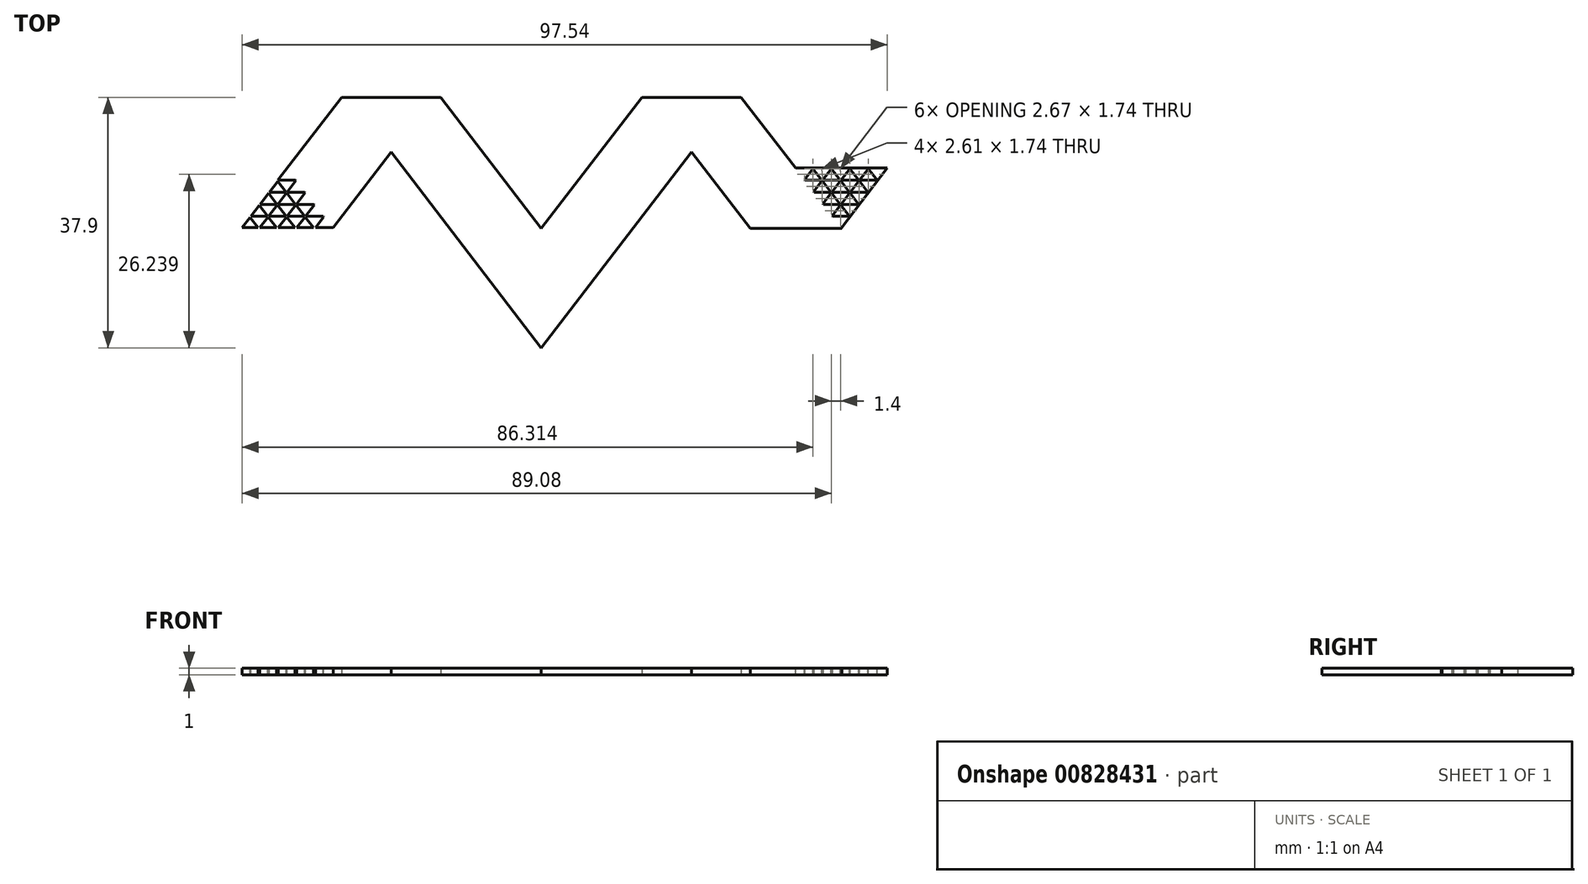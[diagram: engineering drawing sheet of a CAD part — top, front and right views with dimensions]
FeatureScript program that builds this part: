
annotation { "Feature Type Name" : "Feature", "Feature Type Description" : "" }
export const myFeature = defineFeature(function(context is Context, id is Id, definition is map)
    precondition{}
    {
        {
            var Q0;
            Q0=qCreatedBy(makeId("Top.planeOp"),FACE);
            var sketch = newSketch(context, id + "F0", { "sketchPlane" : qUnion([Q0])});
            skLineSegment(sketch, "E0", {"start": v(0, 0) * mm, "end": v(-15.22, 19.83) * mm});
            skLineSegment(sketch, "E1", {"start": v(-15.22, 19.83) * mm, "end": v(-30.22, 19.83) * mm});
            skLineSegment(sketch, "E2", {"start": v(-30.22, 19.83) * mm, "end": v(-45.44, 0) * mm});
            skLineSegment(sketch, "E3", {"start": v(-45.44, 0) * mm, "end": v(-30.44, 0) * mm});
            skPoint(sketch, "E4.endSnap0", {"position": v(-22.72, 19.83) * mm});
            skLineSegment(sketch, "E5.0", {"start": v(1.4, -19.9) * mm, "end": v(-23.55, 12.62) * mm});
            skLineSegment(sketch, "E6.0", {"start": v(-21.05, 13.7) * mm, "end": v(-36.27, -6.12) * mm});
            skLineSegment(sketch, "E7.MirrorCS", {"start": v(21.05, 13.7) * mm, "end": v(36.27, -6.12) * mm});
            skPoint(sketch, "E8.MirrorP", {"position": v(22.72, 19.83) * mm});
            skLineSegment(sketch, "E9.MirrorCS", {"start": v(45.44, 0) * mm, "end": v(30.44, 0) * mm});
            skLineSegment(sketch, "E10.MirrorCS", {"start": v(15.22, 19.83) * mm, "end": v(30.22, 19.83) * mm});
            skLineSegment(sketch, "E11.MirrorCS", {"start": v(-1.4, -19.9) * mm, "end": v(23.55, 12.62) * mm});
            skLineSegment(sketch, "E12.MirrorCS", {"start": v(0, 0) * mm, "end": v(15.22, 19.83) * mm});
            skLineSegment(sketch, "E13.MirrorCS", {"start": v(30.22, 19.83) * mm, "end": v(45.44, 0) * mm});
            skSolve(sketch);
        }
        {
            var Q0;
            Q0=makeQuery(id+"F0.imprint","IMPRINT",FACE,{"disambiguationData":[TD([[makeQuery(id+"F0.imprint","IMPRINT",EDGE,{"derivedFrom":sQuery(id+"F0.wireOp",EDGE,"E0")}),1.0]])]});
            extrude(context, id + "F1", {"entities" : qUnion([Q0]), "depth" : 1 * mm, "offsetDistance" : 25 * mm});
        }
        {
            var Q0;
            Q0=makeQuery(id+"F1.opExtrude","CAP_FACE",FACE,{"disambiguationData":[OSD([sQuery(id+"F0.wireOp",EDGE,"E0"),sQuery(id+"F0.wireOp",EDGE,"E1"),sQuery(id+"F0.wireOp",EDGE,"E2"),sQuery(id+"F0.wireOp",EDGE,"E3"),sQuery(id+"F0.wireOp",EDGE,"E5.0"),sQuery(id+"F0.wireOp",EDGE,"E6.0"),sQuery(id+"F0.wireOp",EDGE,"E7.MirrorCS"),sQuery(id+"F0.wireOp",EDGE,"E9.MirrorCS"),sQuery(id+"F0.wireOp",EDGE,"E10.MirrorCS"),sQuery(id+"F0.wireOp",EDGE,"E11.MirrorCS"),sQuery(id+"F0.wireOp",EDGE,"E12.MirrorCS"),sQuery(id+"F0.wireOp",EDGE,"E13.MirrorCS")])],"isStart":false});
            var sketch = newSketch(context, id + "F2", { "sketchPlane" : qUnion([Q0])});
            skLineSegment(sketch, "E14.1", {"start": v(-30.22, 19.83) * mm, "end": v(-45.44, 0) * mm});
            skLineSegment(sketch, "E14.2", {"start": v(-45.44, 0) * mm, "end": v(-31.57, 0) * mm});
            skPoint(sketch, "E14.3", {"position": v(-38.5, 0) * mm});
            skLineSegment(sketch, "E15.0", {"start": v(-22.72, 11.54) * mm, "end": v(-31.57, 0) * mm});
            skLineSegment(sketch, "E16", {"start": v(-44.04, 0) * mm, "end": v(-44.04, 13.08) * mm, "construction": true});
            skLineSegment(sketch, "E17", {"start": v(-42.64, 0) * mm, "end": v(-42.64, 13.5) * mm, "construction": true});
            skLineSegment(sketch, "E18", {"start": v(-41.24, 0) * mm, "end": v(-41.24, 16.53) * mm, "construction": true});
            skLineSegment(sketch, "E19.MirrorCS", {"start": v(-57.86, 19.83) * mm, "end": v(-42.64, 0) * mm});
            skLineSegment(sketch, "E20.MirrorCS", {"start": v(-55.06, 19.83) * mm, "end": v(-39.84, 0) * mm});
            skLineSegment(sketch, "E21.MirrorCS", {"start": v(-52.26, 19.83) * mm, "end": v(-37.04, 0) * mm});
            skLineSegment(sketch, "E22", {"start": v(-44.04, 1.82) * mm, "end": v(-41.24, 1.82) * mm});
            skLineSegment(sketch, "E23", {"start": v(-42.64, 3.65) * mm, "end": v(-39.84, 3.65) * mm});
            skLineSegment(sketch, "E24", {"start": v(-39.84, 3.65) * mm, "end": v(-41.24, 1.82) * mm});
            skLineSegment(sketch, "E25", {"start": v(-41.24, 1.82) * mm, "end": v(-38.44, 1.82) * mm});
            skLineSegment(sketch, "E26", {"start": v(-39.84, 0) * mm, "end": v(-39.84, 8.29) * mm, "construction": true});
            skLineSegment(sketch, "E27", {"start": v(-38.44, 0) * mm, "end": v(-38.44, 8.1) * mm, "construction": true});
            skLineSegment(sketch, "E28.MirrorCS", {"start": v(-49.46, 19.83) * mm, "end": v(-34.24, 0) * mm});
            skLineSegment(sketch, "E29.MirrorCS", {"start": v(-46.66, 19.83) * mm, "end": v(-31.44, 0) * mm});
            skLineSegment(sketch, "E30", {"start": v(-42.64, 0) * mm, "end": v(-41.24, 1.82) * mm});
            skLineSegment(sketch, "E31", {"start": v(-39.84, 0) * mm, "end": v(-38.44, 1.82) * mm});
            skLineSegment(sketch, "E32", {"start": v(-39.84, 3.65) * mm, "end": v(-38.44, 5.47) * mm});
            skLineSegment(sketch, "E33", {"start": v(-38.44, 5.47) * mm, "end": v(-41.24, 5.47) * mm});
            skLineSegment(sketch, "E34", {"start": v(-39.84, 7.3) * mm, "end": v(-37.04, 7.3) * mm});
            skLineSegment(sketch, "E35", {"start": v(-37.04, 7.3) * mm, "end": v(-38.44, 5.47) * mm});
            skLineSegment(sketch, "E36", {"start": v(-35.64, 5.47) * mm, "end": v(-38.44, 5.47) * mm});
            skLineSegment(sketch, "E37", {"start": v(-35.64, 5.47) * mm, "end": v(-38.44, 1.82) * mm});
            skLineSegment(sketch, "E38", {"start": v(-39.84, 3.65) * mm, "end": v(-34.24, 3.65) * mm});
            skLineSegment(sketch, "E39", {"start": v(-34.24, 3.65) * mm, "end": v(-37.04, 0) * mm});
            skLineSegment(sketch, "E40", {"start": v(-38.44, 1.82) * mm, "end": v(-32.84, 1.82) * mm});
            skLineSegment(sketch, "E41", {"start": v(-32.84, 1.82) * mm, "end": v(-34.24, 0) * mm});
            skLineSegment(sketch, "E42.MirrorCS", {"start": v(42.5, 7.3) * mm, "end": v(45.3, 7.3) * mm});
            skLineSegment(sketch, "E43.MirrorCS", {"start": v(45.3, 3.65) * mm, "end": v(42.5, 3.65) * mm});
            skLineSegment(sketch, "E44.MirrorCS", {"start": v(43.9, 5.47) * mm, "end": v(42.5, 7.3) * mm});
            skLineSegment(sketch, "E45.MirrorCS", {"start": v(43.9, 5.47) * mm, "end": v(45.3, 3.65) * mm});
            skLineSegment(sketch, "E46.MirrorCS", {"start": v(39.7, 7.3) * mm, "end": v(42.5, 7.3) * mm});
            skLineSegment(sketch, "E47.MirrorCS", {"start": v(46.7, 1.82) * mm, "end": v(45.3, 3.65) * mm});
            skLineSegment(sketch, "E48.MirrorCS", {"start": v(43.9, 9.12) * mm, "end": v(45.3, 7.3) * mm});
            skLineSegment(sketch, "E49.MirrorCS", {"start": v(43.9, 1.82) * mm, "end": v(46.7, 1.82) * mm});
            skLineSegment(sketch, "E50.MirrorCS", {"start": v(41.1, 9.12) * mm, "end": v(42.5, 7.3) * mm});
            skLineSegment(sketch, "E51.MirrorCS", {"start": v(45.3, 7.3) * mm, "end": v(50.9, 7.3) * mm});
            skLineSegment(sketch, "E52.MirrorCS", {"start": v(48.1, 3.65) * mm, "end": v(45.3, 3.65) * mm});
            skLineSegment(sketch, "E53.MirrorCS", {"start": v(50.9, 7.3) * mm, "end": v(49.5, 9.12) * mm});
            skLineSegment(sketch, "E54.MirrorCS", {"start": v(43.9, 9.12) * mm, "end": v(43.9, 0.84) * mm, "construction": true});
            skLineSegment(sketch, "E55.MirrorCS", {"start": v(38.3, 9.12) * mm, "end": v(52.3, 9.12) * mm});
            skLineSegment(sketch, "E56.MirrorCS", {"start": v(49.5, 5.47) * mm, "end": v(46.7, 9.12) * mm});
            skLineSegment(sketch, "E57.MirrorCS", {"start": v(45.3, 9.12) * mm, "end": v(45.3, 1.03) * mm, "construction": true});
            skLineSegment(sketch, "E58.MirrorCS", {"start": v(48.1, 3.65) * mm, "end": v(45.3, 7.3) * mm});
            skLineSegment(sketch, "E59.MirrorCS", {"start": v(43.9, 5.47) * mm, "end": v(49.5, 5.47) * mm});
            skLineSegment(sketch, "E60.MirrorCS", {"start": v(42.5, 9.12) * mm, "end": v(42.5, 0) * mm, "construction": true});
            skLineSegment(sketch, "E61.MirrorCS", {"start": v(41.1, 5.47) * mm, "end": v(43.9, 5.47) * mm});
            skLineSegment(sketch, "E62.MirrorCS", {"start": v(22.72, 11.54) * mm, "end": v(31.57, 0) * mm});
            skLineSegment(sketch, "E63.MirrorCS", {"start": v(41.1, 9.12) * mm, "end": v(41.1, 5.47) * mm, "construction": true});
            skLineSegment(sketch, "E64.MirrorCS", {"start": v(41.1, 1.82) * mm, "end": v(46.7, 9.12) * mm});
            skLineSegment(sketch, "E65.MirrorCS", {"start": v(53.52, -10.71) * mm, "end": v(38.3, 9.12) * mm});
            skLineSegment(sketch, "E66.MirrorCS", {"start": v(42.5, 0) * mm, "end": v(49.5, 9.12) * mm});
            skLineSegment(sketch, "E67.MirrorCS", {"start": v(39.7, 7.3) * mm, "end": v(41.1, 9.12) * mm});
            skLineSegment(sketch, "E68.MirrorCS", {"start": v(39.7, 9.12) * mm, "end": v(39.7, 7.3) * mm, "construction": true});
            skPoint(sketch, "E69.MirrorP", {"position": v(45.24, 9.12) * mm});
            skLineSegment(sketch, "E70.MirrorCS", {"start": v(45.3, 0) * mm, "end": v(52.3, 9.12) * mm});
            skLineSegment(sketch, "E71.MirrorCS", {"start": v(41.1, 5.47) * mm, "end": v(43.9, 9.12) * mm});
            skPoint(sketch, "E72.orphan", {"position": v(46.66, 19.83) * mm});
            skPoint(sketch, "E73.orphan", {"position": v(49.46, 19.83) * mm});
            skPoint(sketch, "E74.orphan", {"position": v(52.26, 19.83) * mm});
            skPoint(sketch, "E75.orphan", {"position": v(55.06, 19.83) * mm});
            skPoint(sketch, "E76.orphan", {"position": v(57.86, 19.83) * mm});
            skPoint(sketch, "E77.orphan", {"position": v(41.24, 16.53) * mm});
            skPoint(sketch, "E78.orphan", {"position": v(41.1, -4.38) * mm});
            skPoint(sketch, "E79.orphan", {"position": v(44.04, 13.08) * mm});
            skLineSegment(sketch, "E80", {"start": v(45.3, 0) * mm, "end": v(38.3, 9.12) * mm});
            skLineSegment(sketch, "E81.0", {"start": v(-45.24, 0.1) * mm, "end": v(-31.5, 0.1) * mm});
            skLineSegment(sketch, "E81.1", {"start": v(-30.14, 19.77) * mm, "end": v(-45.24, 0.1) * mm});
            skLineSegment(sketch, "E82.0", {"start": v(-57.94, 19.77) * mm, "end": v(-42.72, -0.06) * mm});
            skLineSegment(sketch, "E83.0", {"start": v(-55.14, 19.77) * mm, "end": v(-39.92, -0.06) * mm});
            skLineSegment(sketch, "E84.0", {"start": v(-52.34, 19.77) * mm, "end": v(-37.12, -0.06) * mm});
            skLineSegment(sketch, "E85.0", {"start": v(-49.54, 19.77) * mm, "end": v(-34.32, -0.06) * mm});
            skLineSegment(sketch, "E86.0", {"start": v(-46.74, 19.77) * mm, "end": v(-31.52, -0.06) * mm});
            skLineSegment(sketch, "E87.0", {"start": v(-38.44, 5.57) * mm, "end": v(-41.24, 5.57) * mm});
            skLineSegment(sketch, "E87.1", {"start": v(-35.64, 5.57) * mm, "end": v(-38.44, 5.57) * mm});
            skLineSegment(sketch, "E88.0", {"start": v(-39.84, 3.55) * mm, "end": v(-34.24, 3.55) * mm});
            skLineSegment(sketch, "E88.1", {"start": v(-42.64, 3.55) * mm, "end": v(-39.84, 3.55) * mm});
            skLineSegment(sketch, "E89.0", {"start": v(-38.44, 1.72) * mm, "end": v(-32.84, 1.72) * mm});
            skLineSegment(sketch, "E89.1", {"start": v(-41.24, 1.72) * mm, "end": v(-38.44, 1.72) * mm});
            skLineSegment(sketch, "E89.2", {"start": v(-44.04, 1.72) * mm, "end": v(-41.24, 1.72) * mm});
            skLineSegment(sketch, "E90.0", {"start": v(41.02, 9.06) * mm, "end": v(46.64, 1.74) * mm});
            skLineSegment(sketch, "E91.0", {"start": v(43.82, 9.06) * mm, "end": v(48.04, 3.57) * mm});
            skLineSegment(sketch, "E92.0", {"start": v(49.42, 5.41) * mm, "end": v(46.62, 9.06) * mm});
            skLineSegment(sketch, "E93.0", {"start": v(50.82, 7.24) * mm, "end": v(49.42, 9.06) * mm});
            skSolve(sketch);
        }
        {
            var Q0;
            {var subQ0=sQuery(id+"F2.wireOp",EDGE,"E81.0");var subQ3=sQuery(id+"F2.wireOp",EDGE,"E31");var subQ4=makeQuery(id+"F2.imprint","INTERSECT",VERTEX,{"derivedFrom":[subQ3,subQ0]});Q0=makeQuery(id+"F2.imprint","IMPRINT",FACE,{"disambiguationData":[TD([[makeQuery(id+"F2.imprint","IMPRINT",EDGE,{"disambiguationData":[TD([[subQ4,-1.0]])],"derivedFrom":subQ3}),1.0]])]});}
            var Q1;
            {var subQ3=sQuery(id+"F2.wireOp",EDGE,"E33");var subQ7=sQuery(id+"F2.wireOp",EDGE,"E85.0");var subQ9=makeQuery(id+"F2.imprint","INTERSECT",VERTEX,{"derivedFrom":[subQ3,subQ7]});Q1=makeQuery(id+"F2.imprint","IMPRINT",FACE,{"disambiguationData":[TD([[makeQuery(id+"F2.imprint","IMPRINT",EDGE,{"disambiguationData":[TD([[subQ9,-1.0]])],"derivedFrom":subQ3}),1.0]])]});}
            var Q2;
            {var subQ0=sQuery(id+"F2.wireOp",EDGE,"E81.1");var subQ3=sQuery(id+"F2.wireOp",EDGE,"E34");var subQ4=makeQuery(id+"F2.imprint","INTERSECT",VERTEX,{"derivedFrom":[subQ3,subQ0]});Q2=makeQuery(id+"F2.imprint","IMPRINT",FACE,{"disambiguationData":[TD([[makeQuery(id+"F2.imprint","IMPRINT",EDGE,{"disambiguationData":[TD([[subQ4,-1.0]])],"derivedFrom":subQ3}),-1.0]])]});}
            var Q3;
            {var subQ0=sQuery(id+"F2.wireOp",EDGE,"E36");var subQ5=sQuery(id+"F2.wireOp",EDGE,"E86.0");var subQ6=makeQuery(id+"F2.imprint","INTERSECT",VERTEX,{"derivedFrom":[subQ0,subQ5]});Q3=makeQuery(id+"F2.imprint","IMPRINT",FACE,{"disambiguationData":[TD([[makeQuery(id+"F2.imprint","IMPRINT",EDGE,{"disambiguationData":[TD([[subQ6,-1.0]])],"derivedFrom":subQ5}),-1.0]])]});}
            var Q4;
            {var subQ0=sQuery(id+"F2.wireOp",EDGE,"E89.2");var subQ1=sQuery(id+"F2.wireOp",EDGE,"E19.MirrorCS");var subQ2=makeQuery(id+"F2.imprint","INTERSECT",VERTEX,{"derivedFrom":[subQ1,subQ0]});Q4=makeQuery(id+"F2.imprint","IMPRINT",FACE,{"disambiguationData":[TD([[makeQuery(id+"F2.imprint","IMPRINT",EDGE,{"disambiguationData":[TD([[subQ2,-1.0]])],"derivedFrom":subQ1}),1.0]])]});}
            var Q5;
            {var subQ1=sQuery(id+"F2.wireOp",EDGE,"E20.MirrorCS");var subQ3=sQuery(id+"F2.wireOp",EDGE,"E88.1");var subQ4=makeQuery(id+"F2.imprint","INTERSECT",VERTEX,{"derivedFrom":[subQ1,subQ3]});Q5=makeQuery(id+"F2.imprint","IMPRINT",FACE,{"disambiguationData":[TD([[makeQuery(id+"F2.imprint","IMPRINT",EDGE,{"disambiguationData":[TD([[subQ4,-1.0]])],"derivedFrom":subQ3}),-1.0]])]});}
            var Q6;
            {var subQ1=sQuery(id+"F2.wireOp",EDGE,"E21.MirrorCS");var subQ3=sQuery(id+"F2.wireOp",EDGE,"E88.0");var subQ4=makeQuery(id+"F2.imprint","INTERSECT",VERTEX,{"derivedFrom":[subQ1,subQ3]});Q6=makeQuery(id+"F2.imprint","IMPRINT",FACE,{"disambiguationData":[TD([[makeQuery(id+"F2.imprint","IMPRINT",EDGE,{"disambiguationData":[TD([[subQ4,-1.0]])],"derivedFrom":subQ3}),-1.0]])]});}
            var Q7;
            {var subQ0=sQuery(id+"F2.wireOp",EDGE,"E89.0");var subQ1=sQuery(id+"F2.wireOp",EDGE,"E21.MirrorCS");var subQ2=makeQuery(id+"F2.imprint","INTERSECT",VERTEX,{"derivedFrom":[subQ1,subQ0]});Q7=makeQuery(id+"F2.imprint","IMPRINT",FACE,{"disambiguationData":[TD([[makeQuery(id+"F2.imprint","IMPRINT",EDGE,{"disambiguationData":[TD([[subQ2,-1.0]])],"derivedFrom":subQ1}),1.0]])]});}
            var Q8;
            {var subQ0=sQuery(id+"F2.wireOp",EDGE,"E88.0");var subQ1=sQuery(id+"F2.wireOp",EDGE,"E28.MirrorCS");var subQ2=makeQuery(id+"F2.imprint","INTERSECT",VERTEX,{"derivedFrom":[subQ1,subQ0]});Q8=makeQuery(id+"F2.imprint","IMPRINT",FACE,{"disambiguationData":[TD([[makeQuery(id+"F2.imprint","IMPRINT",EDGE,{"disambiguationData":[TD([[subQ2,-1.0]])],"derivedFrom":subQ0}),-1.0]])]});}
            var Q9;
            {var subQ0=sQuery(id+"F2.wireOp",EDGE,"E89.0");var subQ1=sQuery(id+"F2.wireOp",EDGE,"E28.MirrorCS");var subQ2=makeQuery(id+"F2.imprint","INTERSECT",VERTEX,{"derivedFrom":[subQ1,subQ0]});Q9=makeQuery(id+"F2.imprint","IMPRINT",FACE,{"disambiguationData":[TD([[makeQuery(id+"F2.imprint","IMPRINT",EDGE,{"disambiguationData":[TD([[subQ2,-1.0]])],"derivedFrom":subQ1}),1.0]])]});}
            extrude(context, id + "F3", {"entities" : qUnion([Q0, Q1, Q2, Q3, Q4, Q5, Q6, Q7, Q8, Q9]), "operationType" : NewBodyOperationType.REMOVE, "oppositeDirection" : true, "depth" : 25 * mm, "offsetDistance" : 25 * mm});
        }
        {
            var Q0;
            {var subQ0=sQuery(id+"F2.wireOp",EDGE,"E90.0");var subQ1=sQuery(id+"F2.wireOp",EDGE,"E49.MirrorCS");var subQ2=makeQuery(id+"F2.imprint","INTERSECT",VERTEX,{"derivedFrom":[subQ1,subQ0]});Q0=makeQuery(id+"F2.imprint","IMPRINT",FACE,{"disambiguationData":[TD([[makeQuery(id+"F2.imprint","IMPRINT",EDGE,{"disambiguationData":[TD([[subQ2,1.0]])],"derivedFrom":subQ1}),-1.0]])]});}
            var Q1;
            {var subQ0=sQuery(id+"F2.wireOp",EDGE,"E90.0");var subQ1=sQuery(id+"F2.wireOp",EDGE,"E43.MirrorCS");var subQ2=makeQuery(id+"F2.imprint","INTERSECT",VERTEX,{"derivedFrom":[subQ1,subQ0]});Q1=makeQuery(id+"F2.imprint","IMPRINT",FACE,{"disambiguationData":[TD([[makeQuery(id+"F2.imprint","IMPRINT",EDGE,{"disambiguationData":[TD([[subQ2,-1.0]])],"derivedFrom":subQ1}),1.0]])]});}
            var Q2;
            {var subQ0=sQuery(id+"F2.wireOp",EDGE,"E90.0");var subQ1=sQuery(id+"F2.wireOp",EDGE,"E61.MirrorCS");var subQ2=makeQuery(id+"F2.imprint","INTERSECT",VERTEX,{"derivedFrom":[subQ1,subQ0]});Q2=makeQuery(id+"F2.imprint","IMPRINT",FACE,{"disambiguationData":[TD([[makeQuery(id+"F2.imprint","IMPRINT",EDGE,{"disambiguationData":[TD([[subQ2,1.0]])],"derivedFrom":subQ1}),-1.0]])]});}
            var Q3;
            {var subQ0=sQuery(id+"F2.wireOp",EDGE,"E90.0");var subQ1=sQuery(id+"F2.wireOp",EDGE,"E46.MirrorCS");var subQ2=makeQuery(id+"F2.imprint","INTERSECT",VERTEX,{"derivedFrom":[subQ1,subQ0]});Q3=makeQuery(id+"F2.imprint","IMPRINT",FACE,{"disambiguationData":[TD([[makeQuery(id+"F2.imprint","IMPRINT",EDGE,{"disambiguationData":[TD([[subQ2,1.0]])],"derivedFrom":subQ1}),-1.0]])]});}
            var Q4;
            {var subQ0=sQuery(id+"F2.wireOp",EDGE,"E67.MirrorCS");var subQ5=makeQuery(id+"F2.imprint","INTERSECT",VERTEX,{"derivedFrom":[subQ0,sQuery(id+"F2.wireOp",EDGE,"E90.0")]});Q4=makeQuery(id+"F2.imprint","IMPRINT",FACE,{"disambiguationData":[TD([[makeQuery(id+"F2.imprint","IMPRINT",EDGE,{"disambiguationData":[TD([[subQ5,1.0]])],"derivedFrom":subQ0}),1.0]])]});}
            var Q5;
            {var subQ0=sQuery(id+"F2.wireOp",EDGE,"E50.MirrorCS");Q5=makeQuery(id+"F2.imprint","IMPRINT",FACE,{"disambiguationData":[TD([[makeQuery(id+"F2.imprint","IMPRINT",EDGE,{"derivedFrom":subQ0}),1.0]])]});}
            var Q6;
            {var subQ0=sQuery(id+"F2.wireOp",EDGE,"E44.MirrorCS");Q6=makeQuery(id+"F2.imprint","IMPRINT",FACE,{"disambiguationData":[TD([[makeQuery(id+"F2.imprint","IMPRINT",EDGE,{"derivedFrom":subQ0}),-1.0]])]});}
            var Q7;
            {var subQ0=sQuery(id+"F2.wireOp",EDGE,"E48.MirrorCS");Q7=makeQuery(id+"F2.imprint","IMPRINT",FACE,{"disambiguationData":[TD([[makeQuery(id+"F2.imprint","IMPRINT",EDGE,{"derivedFrom":subQ0}),1.0]])]});}
            var Q8;
            {var subQ0=sQuery(id+"F2.wireOp",EDGE,"E66.MirrorCS");var subQ5=makeQuery(id+"F2.imprint","INTERSECT",VERTEX,{"derivedFrom":[subQ0,sQuery(id+"F2.wireOp",EDGE,"E93.0")]});Q8=makeQuery(id+"F2.imprint","IMPRINT",FACE,{"disambiguationData":[TD([[makeQuery(id+"F2.imprint","IMPRINT",EDGE,{"disambiguationData":[TD([[subQ5,1.0]])],"derivedFrom":subQ0}),1.0]])]});}
            var Q9;
            {var subQ0=sQuery(id+"F2.wireOp",EDGE,"E53.MirrorCS");Q9=makeQuery(id+"F2.imprint","IMPRINT",FACE,{"disambiguationData":[TD([[makeQuery(id+"F2.imprint","IMPRINT",EDGE,{"derivedFrom":subQ0}),-1.0]])]});}
            var Q10;
            {var subQ0=sQuery(id+"F2.wireOp",EDGE,"E51.MirrorCS");var subQ1=makeQuery(id+"F2.imprint","INTERSECT",VERTEX,{"derivedFrom":[subQ0,sQuery(id+"F2.wireOp",EDGE,"E93.0")]});Q10=makeQuery(id+"F2.imprint","IMPRINT",FACE,{"disambiguationData":[TD([[makeQuery(id+"F2.imprint","IMPRINT",EDGE,{"disambiguationData":[TD([[subQ1,1.0]])],"derivedFrom":subQ0}),-1.0]])]});}
            var Q11;
            {var subQ3=sQuery(id+"F2.wireOp",EDGE,"E59.MirrorCS");var subQ6=makeQuery(id+"F2.imprint","INTERSECT",VERTEX,{"derivedFrom":[subQ3,sQuery(id+"F2.wireOp",EDGE,"E92.0")]});Q11=makeQuery(id+"F2.imprint","IMPRINT",FACE,{"disambiguationData":[TD([[makeQuery(id+"F2.imprint","IMPRINT",EDGE,{"disambiguationData":[TD([[subQ6,1.0]])],"derivedFrom":subQ3}),-1.0]])]});}
            var Q12;
            {var subQ1=sQuery(id+"F2.wireOp",EDGE,"E51.MirrorCS");var subQ3=sQuery(id+"F2.wireOp",EDGE,"E92.0");var subQ4=makeQuery(id+"F2.imprint","INTERSECT",VERTEX,{"derivedFrom":[subQ1,subQ3]});Q12=makeQuery(id+"F2.imprint","IMPRINT",FACE,{"disambiguationData":[TD([[makeQuery(id+"F2.imprint","IMPRINT",EDGE,{"disambiguationData":[TD([[subQ4,1.0]])],"derivedFrom":subQ3}),1.0]])]});}
            var Q13;
            {var subQ0=sQuery(id+"F2.wireOp",EDGE,"E45.MirrorCS");Q13=makeQuery(id+"F2.imprint","IMPRINT",FACE,{"disambiguationData":[TD([[makeQuery(id+"F2.imprint","IMPRINT",EDGE,{"derivedFrom":subQ0}),1.0]])]});}
            var Q14;
            {var subQ0=sQuery(id+"F2.wireOp",EDGE,"E47.MirrorCS");Q14=makeQuery(id+"F2.imprint","IMPRINT",FACE,{"disambiguationData":[TD([[makeQuery(id+"F2.imprint","IMPRINT",EDGE,{"derivedFrom":subQ0}),-1.0]])]});}
            var Q15;
            {var subQ0=sQuery(id+"F2.wireOp",EDGE,"E47.MirrorCS");Q15=makeQuery(id+"F2.imprint","IMPRINT",FACE,{"disambiguationData":[TD([[makeQuery(id+"F2.imprint","IMPRINT",EDGE,{"derivedFrom":subQ0}),1.0]])]});}
            var Q16;
            {var subQ1=sQuery(id+"F2.wireOp",EDGE,"E43.MirrorCS");var subQ3=sQuery(id+"F2.wireOp",EDGE,"E90.0");var subQ4=makeQuery(id+"F2.imprint","INTERSECT",VERTEX,{"derivedFrom":[subQ1,subQ3]});Q16=makeQuery(id+"F2.imprint","IMPRINT",FACE,{"disambiguationData":[TD([[makeQuery(id+"F2.imprint","IMPRINT",EDGE,{"disambiguationData":[TD([[subQ4,-1.0]])],"derivedFrom":subQ3}),1.0]])]});}
            var Q17;
            {var subQ0=sQuery(id+"F2.wireOp",EDGE,"E45.MirrorCS");Q17=makeQuery(id+"F2.imprint","IMPRINT",FACE,{"disambiguationData":[TD([[makeQuery(id+"F2.imprint","IMPRINT",EDGE,{"derivedFrom":subQ0}),-1.0]])]});}
            var Q18;
            {var subQ0=sQuery(id+"F2.wireOp",EDGE,"E70.MirrorCS");var subQ3=sQuery(id+"F2.wireOp",EDGE,"E90.0");var subQ5=makeQuery(id+"F2.imprint","INTERSECT",VERTEX,{"derivedFrom":[subQ0,subQ3]});Q18=makeQuery(id+"F2.imprint","IMPRINT",FACE,{"disambiguationData":[TD([[makeQuery(id+"F2.imprint","IMPRINT",EDGE,{"disambiguationData":[TD([[subQ5,1.0]])],"derivedFrom":subQ3}),1.0]])]});}
            var Q19;
            {var subQ0=sQuery(id+"F2.wireOp",EDGE,"E44.MirrorCS");Q19=makeQuery(id+"F2.imprint","IMPRINT",FACE,{"disambiguationData":[TD([[makeQuery(id+"F2.imprint","IMPRINT",EDGE,{"derivedFrom":subQ0}),1.0]])]});}
            var Q20;
            {var subQ1=sQuery(id+"F2.wireOp",EDGE,"E61.MirrorCS");var subQ3=sQuery(id+"F2.wireOp",EDGE,"E90.0");var subQ4=makeQuery(id+"F2.imprint","INTERSECT",VERTEX,{"derivedFrom":[subQ1,subQ3]});Q20=makeQuery(id+"F2.imprint","IMPRINT",FACE,{"disambiguationData":[TD([[makeQuery(id+"F2.imprint","IMPRINT",EDGE,{"disambiguationData":[TD([[subQ4,-1.0]])],"derivedFrom":subQ3}),1.0]])]});}
            var Q21;
            {var subQ1=sQuery(id+"F2.wireOp",EDGE,"E52.MirrorCS");var subQ3=sQuery(id+"F2.wireOp",EDGE,"E91.0");var subQ4=makeQuery(id+"F2.imprint","INTERSECT",VERTEX,{"derivedFrom":[subQ1,subQ3]});Q21=makeQuery(id+"F2.imprint","IMPRINT",FACE,{"disambiguationData":[TD([[makeQuery(id+"F2.imprint","IMPRINT",EDGE,{"disambiguationData":[TD([[subQ4,1.0]])],"derivedFrom":subQ3}),1.0]])]});}
            var Q22;
            {var subQ0=sQuery(id+"F2.wireOp",EDGE,"E91.0");var subQ1=sQuery(id+"F2.wireOp",EDGE,"E59.MirrorCS");var subQ2=makeQuery(id+"F2.imprint","INTERSECT",VERTEX,{"derivedFrom":[subQ1,subQ0]});Q22=makeQuery(id+"F2.imprint","IMPRINT",FACE,{"disambiguationData":[TD([[makeQuery(id+"F2.imprint","IMPRINT",EDGE,{"disambiguationData":[TD([[subQ2,-1.0]])],"derivedFrom":subQ0}),1.0]])]});}
            var Q23;
            {var subQ3=sQuery(id+"F2.wireOp",EDGE,"E59.MirrorCS");var subQ5=sQuery(id+"F2.wireOp",EDGE,"E91.0");var subQ6=makeQuery(id+"F2.imprint","INTERSECT",VERTEX,{"derivedFrom":[subQ3,subQ5]});Q23=makeQuery(id+"F2.imprint","IMPRINT",FACE,{"disambiguationData":[TD([[makeQuery(id+"F2.imprint","IMPRINT",EDGE,{"disambiguationData":[TD([[subQ6,1.0]])],"derivedFrom":subQ5}),1.0]])]});}
            var Q24;
            {var subQ0=sQuery(id+"F2.wireOp",EDGE,"E70.MirrorCS");var subQ3=sQuery(id+"F2.wireOp",EDGE,"E91.0");var subQ5=makeQuery(id+"F2.imprint","INTERSECT",VERTEX,{"derivedFrom":[subQ0,subQ3]});Q24=makeQuery(id+"F2.imprint","IMPRINT",FACE,{"disambiguationData":[TD([[makeQuery(id+"F2.imprint","IMPRINT",EDGE,{"disambiguationData":[TD([[subQ5,1.0]])],"derivedFrom":subQ3}),1.0]])]});}
            var Q25;
            {var subQ0=sQuery(id+"F2.wireOp",EDGE,"E59.MirrorCS");var subQ5=sQuery(id+"F2.wireOp",EDGE,"E92.0");var subQ6=makeQuery(id+"F2.imprint","INTERSECT",VERTEX,{"derivedFrom":[subQ0,subQ5]});Q25=makeQuery(id+"F2.imprint","IMPRINT",FACE,{"disambiguationData":[TD([[makeQuery(id+"F2.imprint","IMPRINT",EDGE,{"disambiguationData":[TD([[subQ6,-1.0]])],"derivedFrom":subQ5}),-1.0]])]});}
            var Q26;
            {var subQ0=sQuery(id+"F2.wireOp",EDGE,"E50.MirrorCS");Q26=makeQuery(id+"F2.imprint","IMPRINT",FACE,{"disambiguationData":[TD([[makeQuery(id+"F2.imprint","IMPRINT",EDGE,{"derivedFrom":subQ0}),-1.0]])]});}
            var Q27;
            {var subQ1=sQuery(id+"F2.wireOp",EDGE,"E46.MirrorCS");var subQ3=sQuery(id+"F2.wireOp",EDGE,"E90.0");var subQ4=makeQuery(id+"F2.imprint","INTERSECT",VERTEX,{"derivedFrom":[subQ1,subQ3]});Q27=makeQuery(id+"F2.imprint","IMPRINT",FACE,{"disambiguationData":[TD([[makeQuery(id+"F2.imprint","IMPRINT",EDGE,{"disambiguationData":[TD([[subQ4,-1.0]])],"derivedFrom":subQ3}),1.0]])]});}
            var Q28;
            {var subQ0=sQuery(id+"F2.wireOp",EDGE,"E48.MirrorCS");Q28=makeQuery(id+"F2.imprint","IMPRINT",FACE,{"disambiguationData":[TD([[makeQuery(id+"F2.imprint","IMPRINT",EDGE,{"derivedFrom":subQ0}),-1.0]])]});}
            var Q29;
            {var subQ1=sQuery(id+"F2.wireOp",EDGE,"E42.MirrorCS");var subQ3=sQuery(id+"F2.wireOp",EDGE,"E91.0");var subQ4=makeQuery(id+"F2.imprint","INTERSECT",VERTEX,{"derivedFrom":[subQ1,subQ3]});Q29=makeQuery(id+"F2.imprint","IMPRINT",FACE,{"disambiguationData":[TD([[makeQuery(id+"F2.imprint","IMPRINT",EDGE,{"disambiguationData":[TD([[subQ4,-1.0]])],"derivedFrom":subQ3}),1.0]])]});}
            var Q30;
            {var subQ0=sQuery(id+"F2.wireOp",EDGE,"E92.0");var subQ5=sQuery(id+"F2.wireOp",EDGE,"E64.MirrorCS");var subQ7=makeQuery(id+"F2.imprint","INTERSECT",VERTEX,{"derivedFrom":[subQ5,subQ0]});Q30=makeQuery(id+"F2.imprint","IMPRINT",FACE,{"disambiguationData":[TD([[makeQuery(id+"F2.imprint","IMPRINT",EDGE,{"disambiguationData":[TD([[subQ7,1.0]])],"derivedFrom":subQ0}),-1.0]])]});}
            var Q31;
            {var subQ0=sQuery(id+"F2.wireOp",EDGE,"E92.0");var subQ1=sQuery(id+"F2.wireOp",EDGE,"E51.MirrorCS");var subQ2=makeQuery(id+"F2.imprint","INTERSECT",VERTEX,{"derivedFrom":[subQ1,subQ0]});Q31=makeQuery(id+"F2.imprint","IMPRINT",FACE,{"disambiguationData":[TD([[makeQuery(id+"F2.imprint","IMPRINT",EDGE,{"disambiguationData":[TD([[subQ2,1.0]])],"derivedFrom":subQ0}),-1.0]])]});}
            var Q32;
            {var subQ0=sQuery(id+"F2.wireOp",EDGE,"E53.MirrorCS");Q32=makeQuery(id+"F2.imprint","IMPRINT",FACE,{"disambiguationData":[TD([[makeQuery(id+"F2.imprint","IMPRINT",EDGE,{"derivedFrom":subQ0}),1.0]])]});}
            extrude(context, id + "F4", {"entities" : qUnion([Q0, Q1, Q2, Q3, Q4, Q5, Q6, Q7, Q8, Q9, Q10, Q11, Q12, Q13, Q14, Q15, Q16, Q17, Q18, Q19, Q20, Q21, Q22, Q23, Q24, Q25, Q26, Q27, Q28, Q29, Q30, Q31, Q32]), "operationType" : NewBodyOperationType.ADD, "oppositeDirection" : true, "depth" : 1 * mm, "offsetDistance" : 25 * mm});
        }
        {
            var Q0;
            {var subQ5=sQuery(id+"F2.wireOp",EDGE,"E14.2");var subQ6=sQuery(id+"F2.wireOp",EDGE,"E14.1");var subQ7=makeQuery(id+"F2.imprint","INTERSECT",VERTEX,{"derivedFrom":[subQ6,subQ5]});Q0=makeQuery(id+"F2.imprint","IMPRINT",FACE,{"disambiguationData":[TD([[makeQuery(id+"F2.imprint","IMPRINT",EDGE,{"disambiguationData":[TD([[subQ7,1.0]])],"derivedFrom":subQ6}),1.0]])]});}
            var Q1;
            {var subQ0=sQuery(id+"F2.wireOp",EDGE,"E81.1");var subQ1=makeQuery(id+"F2.imprint","INTERSECT",VERTEX,{"derivedFrom":[subQ0,sQuery(id+"F2.wireOp",EDGE,"E89.2")]});Q1=makeQuery(id+"F2.imprint","IMPRINT",FACE,{"disambiguationData":[TD([[makeQuery(id+"F2.imprint","IMPRINT",EDGE,{"disambiguationData":[TD([[subQ1,1.0]])],"derivedFrom":subQ0}),-1.0]])]});}
            var Q2;
            {var subQ1=sQuery(id+"F2.wireOp",EDGE,"E19.MirrorCS");var subQ3=sQuery(id+"F2.wireOp",EDGE,"E81.1");var subQ4=makeQuery(id+"F2.imprint","INTERSECT",VERTEX,{"derivedFrom":[subQ1,subQ3]});Q2=makeQuery(id+"F2.imprint","IMPRINT",FACE,{"disambiguationData":[TD([[makeQuery(id+"F2.imprint","IMPRINT",EDGE,{"disambiguationData":[TD([[subQ4,1.0]])],"derivedFrom":subQ3}),-1.0]])]});}
            var Q3;
            {var subQ0=sQuery(id+"F2.wireOp",EDGE,"E22");var subQ5=sQuery(id+"F2.wireOp",EDGE,"E81.1");var subQ6=makeQuery(id+"F2.imprint","INTERSECT",VERTEX,{"derivedFrom":[subQ0,subQ5]});Q3=makeQuery(id+"F2.imprint","IMPRINT",FACE,{"disambiguationData":[TD([[makeQuery(id+"F2.imprint","IMPRINT",EDGE,{"disambiguationData":[TD([[subQ6,1.0]])],"derivedFrom":subQ5}),-1.0]])]});}
            var Q4;
            {var subQ0=sQuery(id+"F2.wireOp",EDGE,"E19.MirrorCS");var subQ5=sQuery(id+"F2.wireOp",EDGE,"E81.0");var subQ6=makeQuery(id+"F2.imprint","INTERSECT",VERTEX,{"derivedFrom":[subQ0,subQ5]});Q4=makeQuery(id+"F2.imprint","IMPRINT",FACE,{"disambiguationData":[TD([[makeQuery(id+"F2.imprint","IMPRINT",EDGE,{"disambiguationData":[TD([[subQ6,1.0]])],"derivedFrom":subQ5}),-1.0]])]});}
            var Q5;
            {var subQ1=sQuery(id+"F2.wireOp",EDGE,"E19.MirrorCS");var subQ3=sQuery(id+"F2.wireOp",EDGE,"E81.0");var subQ4=makeQuery(id+"F2.imprint","INTERSECT",VERTEX,{"derivedFrom":[subQ1,subQ3]});Q5=makeQuery(id+"F2.imprint","IMPRINT",FACE,{"disambiguationData":[TD([[makeQuery(id+"F2.imprint","IMPRINT",EDGE,{"disambiguationData":[TD([[subQ4,-1.0]])],"derivedFrom":subQ3}),-1.0]])]});}
            var Q6;
            {var subQ0=sQuery(id+"F2.wireOp",EDGE,"E30");var subQ5=sQuery(id+"F2.wireOp",EDGE,"E81.0");var subQ6=makeQuery(id+"F2.imprint","INTERSECT",VERTEX,{"derivedFrom":[subQ0,subQ5]});Q6=makeQuery(id+"F2.imprint","IMPRINT",FACE,{"disambiguationData":[TD([[makeQuery(id+"F2.imprint","IMPRINT",EDGE,{"disambiguationData":[TD([[subQ6,-1.0]])],"derivedFrom":subQ5}),-1.0]])]});}
            var Q7;
            {var subQ0=sQuery(id+"F2.wireOp",EDGE,"E20.MirrorCS");var subQ5=sQuery(id+"F2.wireOp",EDGE,"E81.0");var subQ7=makeQuery(id+"F2.imprint","INTERSECT",VERTEX,{"derivedFrom":[subQ0,subQ5]});Q7=makeQuery(id+"F2.imprint","IMPRINT",FACE,{"disambiguationData":[TD([[makeQuery(id+"F2.imprint","IMPRINT",EDGE,{"disambiguationData":[TD([[subQ7,1.0]])],"derivedFrom":subQ5}),-1.0]])]});}
            var Q8;
            {var subQ1=sQuery(id+"F2.wireOp",EDGE,"E20.MirrorCS");var subQ3=sQuery(id+"F2.wireOp",EDGE,"E81.0");var subQ4=makeQuery(id+"F2.imprint","INTERSECT",VERTEX,{"derivedFrom":[subQ1,subQ3]});Q8=makeQuery(id+"F2.imprint","IMPRINT",FACE,{"disambiguationData":[TD([[makeQuery(id+"F2.imprint","IMPRINT",EDGE,{"disambiguationData":[TD([[subQ4,-1.0]])],"derivedFrom":subQ3}),-1.0]])]});}
            var Q9;
            {var subQ0=sQuery(id+"F2.wireOp",EDGE,"E31");var subQ5=sQuery(id+"F2.wireOp",EDGE,"E81.0");var subQ6=makeQuery(id+"F2.imprint","INTERSECT",VERTEX,{"derivedFrom":[subQ0,subQ5]});Q9=makeQuery(id+"F2.imprint","IMPRINT",FACE,{"disambiguationData":[TD([[makeQuery(id+"F2.imprint","IMPRINT",EDGE,{"disambiguationData":[TD([[subQ6,-1.0]])],"derivedFrom":subQ5}),-1.0]])]});}
            var Q10;
            {var subQ0=sQuery(id+"F2.wireOp",EDGE,"E81.1");var subQ1=makeQuery(id+"F2.imprint","INTERSECT",VERTEX,{"derivedFrom":[subQ0,sQuery(id+"F2.wireOp",EDGE,"E88.1")]});Q10=makeQuery(id+"F2.imprint","IMPRINT",FACE,{"disambiguationData":[TD([[makeQuery(id+"F2.imprint","IMPRINT",EDGE,{"disambiguationData":[TD([[subQ1,1.0]])],"derivedFrom":subQ0}),-1.0]])]});}
            var Q11;
            {var subQ1=sQuery(id+"F2.wireOp",EDGE,"E20.MirrorCS");var subQ3=sQuery(id+"F2.wireOp",EDGE,"E81.1");var subQ4=makeQuery(id+"F2.imprint","INTERSECT",VERTEX,{"derivedFrom":[subQ1,subQ3]});Q11=makeQuery(id+"F2.imprint","IMPRINT",FACE,{"disambiguationData":[TD([[makeQuery(id+"F2.imprint","IMPRINT",EDGE,{"disambiguationData":[TD([[subQ4,1.0]])],"derivedFrom":subQ3}),-1.0]])]});}
            var Q12;
            {var subQ0=sQuery(id+"F2.wireOp",EDGE,"E23");var subQ5=sQuery(id+"F2.wireOp",EDGE,"E81.1");var subQ6=makeQuery(id+"F2.imprint","INTERSECT",VERTEX,{"derivedFrom":[subQ0,subQ5]});Q12=makeQuery(id+"F2.imprint","IMPRINT",FACE,{"disambiguationData":[TD([[makeQuery(id+"F2.imprint","IMPRINT",EDGE,{"disambiguationData":[TD([[subQ6,1.0]])],"derivedFrom":subQ5}),-1.0]])]});}
            var Q13;
            {var subQ0=sQuery(id+"F2.wireOp",EDGE,"E21.MirrorCS");var subQ5=sQuery(id+"F2.wireOp",EDGE,"E81.1");var subQ7=makeQuery(id+"F2.imprint","INTERSECT",VERTEX,{"derivedFrom":[subQ0,subQ5]});Q13=makeQuery(id+"F2.imprint","IMPRINT",FACE,{"disambiguationData":[TD([[makeQuery(id+"F2.imprint","IMPRINT",EDGE,{"disambiguationData":[TD([[subQ7,-1.0]])],"derivedFrom":subQ5}),-1.0]])]});}
            var Q14;
            {var subQ1=sQuery(id+"F2.wireOp",EDGE,"E21.MirrorCS");var subQ3=sQuery(id+"F2.wireOp",EDGE,"E81.1");var subQ4=makeQuery(id+"F2.imprint","INTERSECT",VERTEX,{"derivedFrom":[subQ1,subQ3]});Q14=makeQuery(id+"F2.imprint","IMPRINT",FACE,{"disambiguationData":[TD([[makeQuery(id+"F2.imprint","IMPRINT",EDGE,{"disambiguationData":[TD([[subQ4,1.0]])],"derivedFrom":subQ3}),-1.0]])]});}
            var Q15;
            {var subQ0=sQuery(id+"F2.wireOp",EDGE,"E33");var subQ5=sQuery(id+"F2.wireOp",EDGE,"E81.1");var subQ6=makeQuery(id+"F2.imprint","INTERSECT",VERTEX,{"derivedFrom":[subQ0,subQ5]});Q15=makeQuery(id+"F2.imprint","IMPRINT",FACE,{"disambiguationData":[TD([[makeQuery(id+"F2.imprint","IMPRINT",EDGE,{"disambiguationData":[TD([[subQ6,1.0]])],"derivedFrom":subQ5}),-1.0]])]});}
            var Q16;
            {var subQ0=sQuery(id+"F2.wireOp",EDGE,"E85.0");var subQ1=sQuery(id+"F2.wireOp",EDGE,"E14.1");var subQ2=makeQuery(id+"F2.imprint","INTERSECT",VERTEX,{"derivedFrom":[subQ1,subQ0]});Q16=makeQuery(id+"F2.imprint","IMPRINT",FACE,{"disambiguationData":[TD([[makeQuery(id+"F2.imprint","IMPRINT",EDGE,{"disambiguationData":[TD([[subQ2,-1.0]])],"derivedFrom":subQ1}),1.0]])]});}
            var Q17;
            {var subQ0=sQuery(id+"F2.wireOp",EDGE,"E28.MirrorCS");var subQ5=sQuery(id+"F2.wireOp",EDGE,"E81.1");var subQ6=makeQuery(id+"F2.imprint","INTERSECT",VERTEX,{"derivedFrom":[subQ0,subQ5]});Q17=makeQuery(id+"F2.imprint","IMPRINT",FACE,{"disambiguationData":[TD([[makeQuery(id+"F2.imprint","IMPRINT",EDGE,{"disambiguationData":[TD([[subQ6,-1.0]])],"derivedFrom":subQ5}),-1.0]])]});}
            var Q18;
            {var subQ1=sQuery(id+"F2.wireOp",EDGE,"E28.MirrorCS");var subQ3=sQuery(id+"F2.wireOp",EDGE,"E81.1");var subQ4=makeQuery(id+"F2.imprint","INTERSECT",VERTEX,{"derivedFrom":[subQ1,subQ3]});Q18=makeQuery(id+"F2.imprint","IMPRINT",FACE,{"disambiguationData":[TD([[makeQuery(id+"F2.imprint","IMPRINT",EDGE,{"disambiguationData":[TD([[subQ4,1.0]])],"derivedFrom":subQ3}),-1.0]])]});}
            var Q19;
            {var subQ0=sQuery(id+"F2.wireOp",EDGE,"E21.MirrorCS");var subQ5=sQuery(id+"F2.wireOp",EDGE,"E81.0");var subQ6=makeQuery(id+"F2.imprint","INTERSECT",VERTEX,{"derivedFrom":[subQ0,subQ5]});Q19=makeQuery(id+"F2.imprint","IMPRINT",FACE,{"disambiguationData":[TD([[makeQuery(id+"F2.imprint","IMPRINT",EDGE,{"disambiguationData":[TD([[subQ6,1.0]])],"derivedFrom":subQ5}),-1.0]])]});}
            var Q20;
            {var subQ1=sQuery(id+"F2.wireOp",EDGE,"E21.MirrorCS");var subQ3=sQuery(id+"F2.wireOp",EDGE,"E81.0");var subQ4=makeQuery(id+"F2.imprint","INTERSECT",VERTEX,{"derivedFrom":[subQ1,subQ3]});Q20=makeQuery(id+"F2.imprint","IMPRINT",FACE,{"disambiguationData":[TD([[makeQuery(id+"F2.imprint","IMPRINT",EDGE,{"disambiguationData":[TD([[subQ4,-1.0]])],"derivedFrom":subQ3}),-1.0]])]});}
            var Q21;
            {var subQ0=sQuery(id+"F2.wireOp",EDGE,"E39");var subQ5=sQuery(id+"F2.wireOp",EDGE,"E81.0");var subQ6=makeQuery(id+"F2.imprint","INTERSECT",VERTEX,{"derivedFrom":[subQ0,subQ5]});Q21=makeQuery(id+"F2.imprint","IMPRINT",FACE,{"disambiguationData":[TD([[makeQuery(id+"F2.imprint","IMPRINT",EDGE,{"disambiguationData":[TD([[subQ6,-1.0]])],"derivedFrom":subQ5}),-1.0]])]});}
            var Q22;
            {var subQ0=sQuery(id+"F2.wireOp",EDGE,"E28.MirrorCS");var subQ5=sQuery(id+"F2.wireOp",EDGE,"E81.0");var subQ6=makeQuery(id+"F2.imprint","INTERSECT",VERTEX,{"derivedFrom":[subQ0,subQ5]});Q22=makeQuery(id+"F2.imprint","IMPRINT",FACE,{"disambiguationData":[TD([[makeQuery(id+"F2.imprint","IMPRINT",EDGE,{"disambiguationData":[TD([[subQ6,1.0]])],"derivedFrom":subQ5}),-1.0]])]});}
            var Q23;
            {var subQ1=sQuery(id+"F2.wireOp",EDGE,"E28.MirrorCS");var subQ3=sQuery(id+"F2.wireOp",EDGE,"E81.0");var subQ4=makeQuery(id+"F2.imprint","INTERSECT",VERTEX,{"derivedFrom":[subQ1,subQ3]});Q23=makeQuery(id+"F2.imprint","IMPRINT",FACE,{"disambiguationData":[TD([[makeQuery(id+"F2.imprint","IMPRINT",EDGE,{"disambiguationData":[TD([[subQ4,-1.0]])],"derivedFrom":subQ3}),-1.0]])]});}
            var Q24;
            {var subQ5=sQuery(id+"F2.wireOp",EDGE,"E14.2");var subQ7=sQuery(id+"F2.wireOp",EDGE,"E15.0");var subQ8=makeQuery(id+"F2.imprint","INTERSECT",VERTEX,{"derivedFrom":[subQ5,subQ7]});Q24=makeQuery(id+"F2.imprint","IMPRINT",FACE,{"disambiguationData":[TD([[makeQuery(id+"F2.imprint","IMPRINT",EDGE,{"disambiguationData":[TD([[subQ8,1.0]])],"derivedFrom":subQ7}),-1.0]])]});}
            var Q25;
            {var subQ0=sQuery(id+"F2.wireOp",EDGE,"E81.1");var subQ1=sQuery(id+"F2.wireOp",EDGE,"E19.MirrorCS");var subQ2=makeQuery(id+"F2.imprint","INTERSECT",VERTEX,{"derivedFrom":[subQ1,subQ0]});Q25=makeQuery(id+"F2.imprint","IMPRINT",FACE,{"disambiguationData":[TD([[makeQuery(id+"F2.imprint","IMPRINT",EDGE,{"disambiguationData":[TD([[subQ2,-1.0]])],"derivedFrom":subQ1}),1.0]])]});}
            var Q26;
            {var subQ1=sQuery(id+"F2.wireOp",EDGE,"E22");var subQ3=sQuery(id+"F2.wireOp",EDGE,"E83.0");var subQ4=makeQuery(id+"F2.imprint","INTERSECT",VERTEX,{"derivedFrom":[subQ1,subQ3]});Q26=makeQuery(id+"F2.imprint","IMPRINT",FACE,{"disambiguationData":[TD([[makeQuery(id+"F2.imprint","IMPRINT",EDGE,{"disambiguationData":[TD([[subQ4,-1.0]])],"derivedFrom":subQ3}),1.0]])]});}
            var Q27;
            {var subQ5=sQuery(id+"F2.wireOp",EDGE,"E83.0");var subQ6=sQuery(id+"F2.wireOp",EDGE,"E30");var subQ7=makeQuery(id+"F2.imprint","INTERSECT",VERTEX,{"derivedFrom":[subQ6,subQ5]});Q27=makeQuery(id+"F2.imprint","IMPRINT",FACE,{"disambiguationData":[TD([[makeQuery(id+"F2.imprint","IMPRINT",EDGE,{"disambiguationData":[TD([[subQ7,-1.0]])],"derivedFrom":subQ5}),1.0]])]});}
            var Q28;
            {var subQ0=sQuery(id+"F2.wireOp",EDGE,"E89.1");var subQ1=sQuery(id+"F2.wireOp",EDGE,"E31");var subQ2=makeQuery(id+"F2.imprint","INTERSECT",VERTEX,{"derivedFrom":[subQ1,subQ0]});Q28=makeQuery(id+"F2.imprint","IMPRINT",FACE,{"disambiguationData":[TD([[makeQuery(id+"F2.imprint","IMPRINT",EDGE,{"disambiguationData":[TD([[subQ2,-1.0]])],"derivedFrom":subQ1}),1.0]])]});}
            var Q29;
            {var subQ1=sQuery(id+"F2.wireOp",EDGE,"E25");var subQ3=sQuery(id+"F2.wireOp",EDGE,"E84.0");var subQ4=makeQuery(id+"F2.imprint","INTERSECT",VERTEX,{"derivedFrom":[subQ1,subQ3]});Q29=makeQuery(id+"F2.imprint","IMPRINT",FACE,{"disambiguationData":[TD([[makeQuery(id+"F2.imprint","IMPRINT",EDGE,{"disambiguationData":[TD([[subQ4,-1.0]])],"derivedFrom":subQ3}),1.0]])]});}
            var Q30;
            {var subQ0=sQuery(id+"F2.wireOp",EDGE,"E84.0");var subQ1=sQuery(id+"F2.wireOp",EDGE,"E31");var subQ2=makeQuery(id+"F2.imprint","INTERSECT",VERTEX,{"derivedFrom":[subQ1,subQ0]});Q30=makeQuery(id+"F2.imprint","IMPRINT",FACE,{"disambiguationData":[TD([[makeQuery(id+"F2.imprint","IMPRINT",EDGE,{"disambiguationData":[TD([[subQ2,-1.0]])],"derivedFrom":subQ0}),1.0]])]});}
            var Q31;
            {var subQ3=sQuery(id+"F2.wireOp",EDGE,"E85.0");var subQ5=sQuery(id+"F2.wireOp",EDGE,"E39");var subQ6=makeQuery(id+"F2.imprint","INTERSECT",VERTEX,{"derivedFrom":[subQ5,subQ3]});Q31=makeQuery(id+"F2.imprint","IMPRINT",FACE,{"disambiguationData":[TD([[makeQuery(id+"F2.imprint","IMPRINT",EDGE,{"disambiguationData":[TD([[subQ6,-1.0]])],"derivedFrom":subQ5}),-1.0]])]});}
            var Q32;
            {var subQ0=sQuery(id+"F2.wireOp",EDGE,"E85.0");var subQ1=sQuery(id+"F2.wireOp",EDGE,"E39");var subQ2=makeQuery(id+"F2.imprint","INTERSECT",VERTEX,{"derivedFrom":[subQ1,subQ0]});Q32=makeQuery(id+"F2.imprint","IMPRINT",FACE,{"disambiguationData":[TD([[makeQuery(id+"F2.imprint","IMPRINT",EDGE,{"disambiguationData":[TD([[subQ2,1.0]])],"derivedFrom":subQ0}),1.0]])]});}
            var Q33;
            {var subQ3=sQuery(id+"F2.wireOp",EDGE,"E39");var subQ5=sQuery(id+"F2.wireOp",EDGE,"E85.0");var subQ6=makeQuery(id+"F2.imprint","INTERSECT",VERTEX,{"derivedFrom":[subQ3,subQ5]});Q33=makeQuery(id+"F2.imprint","IMPRINT",FACE,{"disambiguationData":[TD([[makeQuery(id+"F2.imprint","IMPRINT",EDGE,{"disambiguationData":[TD([[subQ6,-1.0]])],"derivedFrom":subQ5}),1.0]])]});}
            var Q34;
            {var subQ0=sQuery(id+"F2.wireOp",EDGE,"E86.0");var subQ1=sQuery(id+"F2.wireOp",EDGE,"E41");var subQ2=makeQuery(id+"F2.imprint","INTERSECT",VERTEX,{"derivedFrom":[subQ1,subQ0]});Q34=makeQuery(id+"F2.imprint","IMPRINT",FACE,{"disambiguationData":[TD([[makeQuery(id+"F2.imprint","IMPRINT",EDGE,{"disambiguationData":[TD([[subQ2,-1.0]])],"derivedFrom":subQ1}),-1.0]])]});}
            var Q35;
            {var subQ5=sQuery(id+"F2.wireOp",EDGE,"E81.1");var subQ9=sQuery(id+"F2.wireOp",EDGE,"E20.MirrorCS");var subQ10=makeQuery(id+"F2.imprint","INTERSECT",VERTEX,{"derivedFrom":[subQ9,subQ5]});Q35=makeQuery(id+"F2.imprint","IMPRINT",FACE,{"disambiguationData":[TD([[makeQuery(id+"F2.imprint","IMPRINT",EDGE,{"disambiguationData":[TD([[subQ10,-1.0]])],"derivedFrom":subQ9}),1.0]])]});}
            var Q36;
            {var subQ1=sQuery(id+"F2.wireOp",EDGE,"E23");var subQ3=sQuery(id+"F2.wireOp",EDGE,"E84.0");var subQ4=makeQuery(id+"F2.imprint","INTERSECT",VERTEX,{"derivedFrom":[subQ1,subQ3]});Q36=makeQuery(id+"F2.imprint","IMPRINT",FACE,{"disambiguationData":[TD([[makeQuery(id+"F2.imprint","IMPRINT",EDGE,{"disambiguationData":[TD([[subQ4,-1.0]])],"derivedFrom":subQ3}),1.0]])]});}
            var Q37;
            {var subQ5=sQuery(id+"F2.wireOp",EDGE,"E84.0");var subQ6=sQuery(id+"F2.wireOp",EDGE,"E24");var subQ7=makeQuery(id+"F2.imprint","INTERSECT",VERTEX,{"derivedFrom":[subQ6,subQ5]});Q37=makeQuery(id+"F2.imprint","IMPRINT",FACE,{"disambiguationData":[TD([[makeQuery(id+"F2.imprint","IMPRINT",EDGE,{"disambiguationData":[TD([[subQ7,-1.0]])],"derivedFrom":subQ5}),1.0]])]});}
            var Q38;
            {var subQ0=sQuery(id+"F2.wireOp",EDGE,"E85.0");var subQ1=sQuery(id+"F2.wireOp",EDGE,"E37");var subQ2=makeQuery(id+"F2.imprint","INTERSECT",VERTEX,{"derivedFrom":[subQ1,subQ0]});Q38=makeQuery(id+"F2.imprint","IMPRINT",FACE,{"disambiguationData":[TD([[makeQuery(id+"F2.imprint","IMPRINT",EDGE,{"disambiguationData":[TD([[subQ2,-1.0]])],"derivedFrom":subQ1}),-1.0]])]});}
            var Q39;
            {var subQ0=sQuery(id+"F2.wireOp",EDGE,"E85.0");var subQ1=sQuery(id+"F2.wireOp",EDGE,"E37");var subQ2=makeQuery(id+"F2.imprint","INTERSECT",VERTEX,{"derivedFrom":[subQ1,subQ0]});Q39=makeQuery(id+"F2.imprint","IMPRINT",FACE,{"disambiguationData":[TD([[makeQuery(id+"F2.imprint","IMPRINT",EDGE,{"disambiguationData":[TD([[subQ2,1.0]])],"derivedFrom":subQ0}),1.0]])]});}
            var Q40;
            {var subQ3=sQuery(id+"F2.wireOp",EDGE,"E37");var subQ5=sQuery(id+"F2.wireOp",EDGE,"E85.0");var subQ6=makeQuery(id+"F2.imprint","INTERSECT",VERTEX,{"derivedFrom":[subQ3,subQ5]});Q40=makeQuery(id+"F2.imprint","IMPRINT",FACE,{"disambiguationData":[TD([[makeQuery(id+"F2.imprint","IMPRINT",EDGE,{"disambiguationData":[TD([[subQ6,-1.0]])],"derivedFrom":subQ5}),1.0]])]});}
            var Q41;
            {var subQ0=sQuery(id+"F2.wireOp",EDGE,"E86.0");var subQ3=sQuery(id+"F2.wireOp",EDGE,"E39");var subQ4=makeQuery(id+"F2.imprint","INTERSECT",VERTEX,{"derivedFrom":[subQ3,subQ0]});Q41=makeQuery(id+"F2.imprint","IMPRINT",FACE,{"disambiguationData":[TD([[makeQuery(id+"F2.imprint","IMPRINT",EDGE,{"disambiguationData":[TD([[subQ4,-1.0]])],"derivedFrom":subQ3}),-1.0]])]});}
            var Q42;
            {var subQ0=sQuery(id+"F2.wireOp",EDGE,"E33");var subQ5=sQuery(id+"F2.wireOp",EDGE,"E85.0");var subQ6=makeQuery(id+"F2.imprint","INTERSECT",VERTEX,{"derivedFrom":[subQ0,subQ5]});Q42=makeQuery(id+"F2.imprint","IMPRINT",FACE,{"disambiguationData":[TD([[makeQuery(id+"F2.imprint","IMPRINT",EDGE,{"disambiguationData":[TD([[subQ6,1.0]])],"derivedFrom":subQ5}),1.0]])]});}
            var Q43;
            {var subQ3=sQuery(id+"F2.wireOp",EDGE,"E87.0");var subQ5=sQuery(id+"F2.wireOp",EDGE,"E87.1");var subQ7=makeQuery(id+"F2.imprint","INTERSECT",VERTEX,{"derivedFrom":[subQ3,subQ5]});Q43=makeQuery(id+"F2.imprint","IMPRINT",FACE,{"disambiguationData":[TD([[makeQuery(id+"F2.imprint","IMPRINT",EDGE,{"disambiguationData":[TD([[subQ7,-1.0]])],"derivedFrom":subQ3}),1.0]])]});}
            var Q44;
            {var subQ1=sQuery(id+"F2.wireOp",EDGE,"E32");var subQ3=sQuery(id+"F2.wireOp",EDGE,"E85.0");var subQ4=makeQuery(id+"F2.imprint","INTERSECT",VERTEX,{"derivedFrom":[subQ1,subQ3]});Q44=makeQuery(id+"F2.imprint","IMPRINT",FACE,{"disambiguationData":[TD([[makeQuery(id+"F2.imprint","IMPRINT",EDGE,{"disambiguationData":[TD([[subQ4,1.0]])],"derivedFrom":subQ3}),1.0]])]});}
            var Q45;
            {var subQ0=sQuery(id+"F2.wireOp",EDGE,"E32");var subQ5=sQuery(id+"F2.wireOp",EDGE,"E85.0");var subQ7=makeQuery(id+"F2.imprint","INTERSECT",VERTEX,{"derivedFrom":[subQ0,subQ5]});Q45=makeQuery(id+"F2.imprint","IMPRINT",FACE,{"disambiguationData":[TD([[makeQuery(id+"F2.imprint","IMPRINT",EDGE,{"disambiguationData":[TD([[subQ7,-1.0]])],"derivedFrom":subQ5}),1.0]])]});}
            var Q46;
            {var subQ5=sQuery(id+"F2.wireOp",EDGE,"E84.0");var subQ6=sQuery(id+"F2.wireOp",EDGE,"E25");var subQ7=makeQuery(id+"F2.imprint","INTERSECT",VERTEX,{"derivedFrom":[subQ6,subQ5]});Q46=makeQuery(id+"F2.imprint","IMPRINT",FACE,{"disambiguationData":[TD([[makeQuery(id+"F2.imprint","IMPRINT",EDGE,{"disambiguationData":[TD([[subQ7,1.0]])],"derivedFrom":subQ5}),1.0]])]});}
            var Q47;
            {var subQ1=sQuery(id+"F2.wireOp",EDGE,"E21.MirrorCS");var subQ3=sQuery(id+"F2.wireOp",EDGE,"E81.1");var subQ4=makeQuery(id+"F2.imprint","INTERSECT",VERTEX,{"derivedFrom":[subQ1,subQ3]});Q47=makeQuery(id+"F2.imprint","IMPRINT",FACE,{"disambiguationData":[TD([[makeQuery(id+"F2.imprint","IMPRINT",EDGE,{"disambiguationData":[TD([[subQ4,-1.0]])],"derivedFrom":subQ3}),1.0]])]});}
            var Q48;
            {var subQ1=sQuery(id+"F2.wireOp",EDGE,"E89.0");var subQ3=sQuery(id+"F2.wireOp",EDGE,"E21.MirrorCS");var subQ4=makeQuery(id+"F2.imprint","INTERSECT",VERTEX,{"derivedFrom":[subQ3,subQ1]});Q48=makeQuery(id+"F2.imprint","IMPRINT",FACE,{"disambiguationData":[TD([[makeQuery(id+"F2.imprint","IMPRINT",EDGE,{"disambiguationData":[TD([[subQ4,-1.0]])],"derivedFrom":subQ3}),-1.0]])]});}
            var Q49;
            {var subQ0=sQuery(id+"F2.wireOp",EDGE,"E89.0");var subQ1=sQuery(id+"F2.wireOp",EDGE,"E28.MirrorCS");var subQ2=makeQuery(id+"F2.imprint","INTERSECT",VERTEX,{"derivedFrom":[subQ1,subQ0]});Q49=makeQuery(id+"F2.imprint","IMPRINT",FACE,{"disambiguationData":[TD([[makeQuery(id+"F2.imprint","IMPRINT",EDGE,{"disambiguationData":[TD([[subQ2,-1.0]])],"derivedFrom":subQ1}),-1.0]])]});}
            var Q50;
            {var subQ3=sQuery(id+"F2.wireOp",EDGE,"E40");var subQ5=sQuery(id+"F2.wireOp",EDGE,"E85.0");var subQ6=makeQuery(id+"F2.imprint","INTERSECT",VERTEX,{"derivedFrom":[subQ3,subQ5]});Q50=makeQuery(id+"F2.imprint","IMPRINT",FACE,{"disambiguationData":[TD([[makeQuery(id+"F2.imprint","IMPRINT",EDGE,{"disambiguationData":[TD([[subQ6,1.0]])],"derivedFrom":subQ5}),1.0]])]});}
            var Q51;
            {var subQ0=sQuery(id+"F2.wireOp",EDGE,"E81.1");var subQ1=sQuery(id+"F2.wireOp",EDGE,"E28.MirrorCS");var subQ2=makeQuery(id+"F2.imprint","INTERSECT",VERTEX,{"derivedFrom":[subQ1,subQ0]});Q51=makeQuery(id+"F2.imprint","IMPRINT",FACE,{"disambiguationData":[TD([[makeQuery(id+"F2.imprint","IMPRINT",EDGE,{"disambiguationData":[TD([[subQ2,-1.0]])],"derivedFrom":subQ1}),-1.0]])]});}
            var Q52;
            {var subQ0=sQuery(id+"F2.wireOp",EDGE,"E81.1");var subQ1=sQuery(id+"F2.wireOp",EDGE,"E20.MirrorCS");var subQ2=makeQuery(id+"F2.imprint","INTERSECT",VERTEX,{"derivedFrom":[subQ1,subQ0]});Q52=makeQuery(id+"F2.imprint","IMPRINT",FACE,{"disambiguationData":[TD([[makeQuery(id+"F2.imprint","IMPRINT",EDGE,{"disambiguationData":[TD([[subQ2,-1.0]])],"derivedFrom":subQ1}),-1.0]])]});}
            var Q53;
            {var subQ3=sQuery(id+"F2.wireOp",EDGE,"E81.1");var subQ5=sQuery(id+"F2.wireOp",EDGE,"E88.1");var subQ6=makeQuery(id+"F2.imprint","INTERSECT",VERTEX,{"derivedFrom":[subQ3,subQ5]});Q53=makeQuery(id+"F2.imprint","IMPRINT",FACE,{"disambiguationData":[TD([[makeQuery(id+"F2.imprint","IMPRINT",EDGE,{"disambiguationData":[TD([[subQ6,-1.0]])],"derivedFrom":subQ3}),1.0]])]});}
            var Q54;
            {var subQ0=sQuery(id+"F2.wireOp",EDGE,"E81.1");var subQ1=sQuery(id+"F2.wireOp",EDGE,"E19.MirrorCS");var subQ2=makeQuery(id+"F2.imprint","INTERSECT",VERTEX,{"derivedFrom":[subQ1,subQ0]});Q54=makeQuery(id+"F2.imprint","IMPRINT",FACE,{"disambiguationData":[TD([[makeQuery(id+"F2.imprint","IMPRINT",EDGE,{"disambiguationData":[TD([[subQ2,-1.0]])],"derivedFrom":subQ1}),-1.0]])]});}
            var Q55;
            {var subQ0=sQuery(id+"F2.wireOp",EDGE,"E89.2");var subQ7=sQuery(id+"F2.wireOp",EDGE,"E19.MirrorCS");var subQ9=makeQuery(id+"F2.imprint","INTERSECT",VERTEX,{"derivedFrom":[subQ7,subQ0]});Q55=makeQuery(id+"F2.imprint","IMPRINT",FACE,{"disambiguationData":[TD([[makeQuery(id+"F2.imprint","IMPRINT",EDGE,{"disambiguationData":[TD([[subQ9,-1.0]])],"derivedFrom":subQ7}),-1.0]])]});}
            var Q56;
            {var subQ1=sQuery(id+"F2.wireOp",EDGE,"E89.1");var subQ3=sQuery(id+"F2.wireOp",EDGE,"E20.MirrorCS");var subQ4=makeQuery(id+"F2.imprint","INTERSECT",VERTEX,{"derivedFrom":[subQ3,subQ1]});Q56=makeQuery(id+"F2.imprint","IMPRINT",FACE,{"disambiguationData":[TD([[makeQuery(id+"F2.imprint","IMPRINT",EDGE,{"disambiguationData":[TD([[subQ4,-1.0]])],"derivedFrom":subQ3}),-1.0]])]});}
            var Q57;
            {var subQ0=sQuery(id+"F2.wireOp",EDGE,"E29.MirrorCS");var subQ1=sQuery(id+"F2.wireOp",EDGE,"E15.0");var subQ2=makeQuery(id+"F2.imprint","INTERSECT",VERTEX,{"derivedFrom":[subQ1,subQ0]});Q57=makeQuery(id+"F2.imprint","IMPRINT",FACE,{"disambiguationData":[TD([[makeQuery(id+"F2.imprint","IMPRINT",EDGE,{"disambiguationData":[TD([[subQ2,-1.0]])],"derivedFrom":subQ1}),-1.0]])]});}
            var Q58;
            {var subQ0=sQuery(id+"F2.wireOp",EDGE,"E81.0");var subQ1=sQuery(id+"F2.wireOp",EDGE,"E15.0");var subQ2=makeQuery(id+"F2.imprint","INTERSECT",VERTEX,{"derivedFrom":[subQ1,subQ0]});Q58=makeQuery(id+"F2.imprint","IMPRINT",FACE,{"disambiguationData":[TD([[makeQuery(id+"F2.imprint","IMPRINT",EDGE,{"disambiguationData":[TD([[subQ2,-1.0]])],"derivedFrom":subQ1}),-1.0]])]});}
            extrude(context, id + "F5", {"entities" : qUnion([Q0, Q1, Q2, Q3, Q4, Q5, Q6, Q7, Q8, Q9, Q10, Q11, Q12, Q13, Q14, Q15, Q16, Q17, Q18, Q19, Q20, Q21, Q22, Q23, Q24, Q25, Q26, Q27, Q28, Q29, Q30, Q31, Q32, Q33, Q34, Q35, Q36, Q37, Q38, Q39, Q40, Q41, Q42, Q43, Q44, Q45, Q46, Q47, Q48, Q49, Q50, Q51, Q52, Q53, Q54, Q55, Q56, Q57, Q58]), "operationType" : NewBodyOperationType.REMOVE, "oppositeDirection" : true, "depth" : 25 * mm, "offsetDistance" : 25 * mm});
        }
    });
